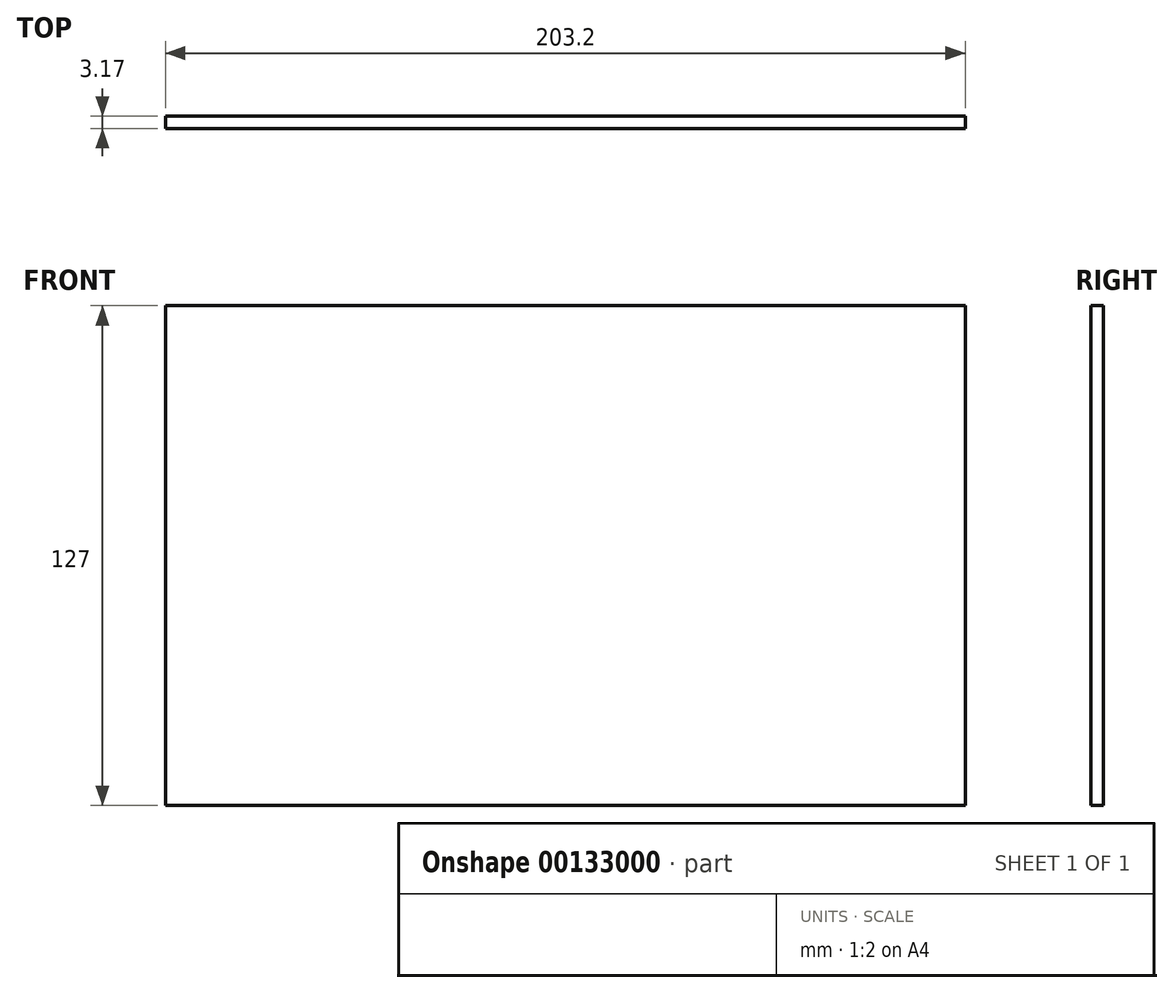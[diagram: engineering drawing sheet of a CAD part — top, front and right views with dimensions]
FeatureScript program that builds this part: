
annotation { "Feature Type Name" : "Feature", "Feature Type Description" : "" }
export const myFeature = defineFeature(function(context is Context, id is Id, definition is map)
    precondition{}
    {
        {
            var Q0;
            Q0=qCreatedBy(makeId("Front.planeOp"),FACE);
            var sketch = newSketch(context, id + "F0", { "sketchPlane" : qUnion([Q0])});
            skLineSegment(sketch, "E0.bottom", {"start": v(0, 0) * mm, "end": v(203.2, 0) * mm});
            skLineSegment(sketch, "E0.top", {"start": v(0, 127) * mm, "end": v(203.2, 127) * mm});
            skLineSegment(sketch, "E0.left", {"start": v(0, 0) * mm, "end": v(0, 127) * mm});
            skLineSegment(sketch, "E0.right", {"start": v(203.2, 0) * mm, "end": v(203.2, 127) * mm});
            skSolve(sketch);
        }
        {
            var Q0;
            Q0 = qSketchRegion(id + "F0", true);
            var Q1;
            Q1=makeQuery(id+"F0.imprint","IMPRINT",FACE,{"disambiguationData":[TD([[makeQuery(id+"F0.imprint","IMPRINT",EDGE,{"derivedFrom":sQuery(id+"F0.wireOp",EDGE,"E0.bottom")}),1.0]])]});
            extrude(context, id + "F1", {"entities" : qUnion([Q0, Q1]), "depth" : 3.17 * mm});
        }
    });
